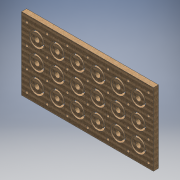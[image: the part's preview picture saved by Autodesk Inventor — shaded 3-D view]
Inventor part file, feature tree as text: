
AUTODESK INVENTOR PART (.ipt)
format: ipt  version: 2016 (Build 200138000, 138)  size: 318,464 bytes
history: native  units: mm
features: extrude x1, sketch x1
ambient origin geometry x8: Origin, YZ Plane, XZ Plane, XY Plane, X Axis, Y Axis, Z Axis, Center Point
bodies: Body1 (feature_tree)
feature tree (2):
  extrude  "Extrusion3"  Depth=5.95mm
  sketch  "Sketch1"  dims[d0=18.0mm d1=2.0mm d2=3.43mm d6=6.35mm d25=40.0mm d27=360.0deg d29=45.0deg d30=12.0mm d31=30.0mm d33=24.0mm d34=10.0mm d36=10.0mm d38=60.0mm d40=24.0mm d41=10.0mm d43=10.0mm d45=6.0mm d46=6.0mm d47=6.0mm d48=6.0mm d49=5.95mm d50=0.0mm]
